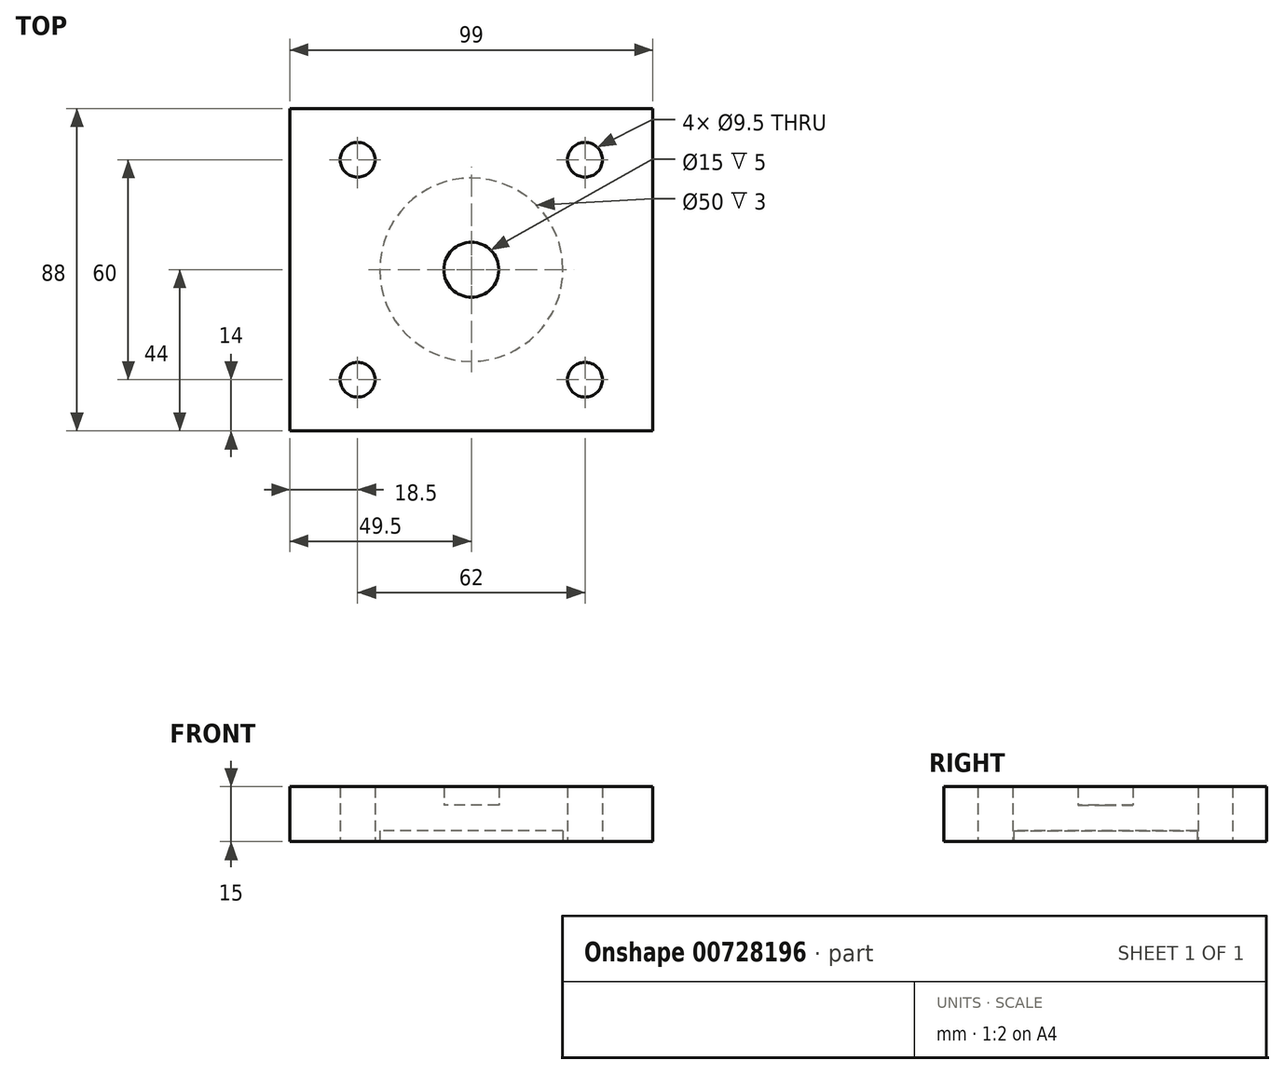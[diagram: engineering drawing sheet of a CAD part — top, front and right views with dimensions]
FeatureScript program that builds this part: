
annotation { "Feature Type Name" : "Feature", "Feature Type Description" : "" }
export const myFeature = defineFeature(function(context is Context, id is Id, definition is map)
    precondition{}
    {
        {
            var Q0;
            Q0=qCreatedBy(makeId("Top.planeOp"),FACE);
            var sketch = newSketch(context, id + "F0", { "sketchPlane" : qUnion([Q0])});
            skLineSegment(sketch, "E0.bottom", {"start": v(49.5, -44) * mm, "end": v(-49.5, -44) * mm});
            skLineSegment(sketch, "E0.top", {"start": v(49.5, 44) * mm, "end": v(-49.5, 44) * mm});
            skLineSegment(sketch, "E0.left", {"start": v(49.5, -44) * mm, "end": v(49.5, 44) * mm});
            skLineSegment(sketch, "E0.right", {"start": v(-49.5, -44) * mm, "end": v(-49.5, 44) * mm});
            skPoint(sketch, "E0.middle", {"position": v(0, 0) * mm});
            skCircle(sketch, "E1", {"center": v(-31, 30) * mm, "radius": 4.75 * mm});
            skCircle(sketch, "E2", {"center": v(31, 30) * mm, "radius": 4.75 * mm});
            skCircle(sketch, "E3.MirrorC", {"center": v(-31, -30) * mm, "radius": 4.75 * mm});
            skCircle(sketch, "E4.MirrorC", {"center": v(31, -30) * mm, "radius": 4.75 * mm});
            skCircle(sketch, "E5", {"center": v(0, 0) * mm, "radius": 7.5 * mm});
            skSolve(sketch);
        }
        {
            var Q0;
            Q0=makeQuery(id+"F0.imprint","IMPRINT",FACE,{"disambiguationData":[TD([[makeQuery(id+"F0.imprint","IMPRINT",EDGE,{"derivedFrom":sQuery(id+"F0.wireOp",EDGE,"E5")}),1.0]])]});
            extrude(context, id + "F1", {"entities" : qUnion([Q0]), "depth" : 10 * mm, "offsetDistance" : 25 * mm});
        }
        {
            var Q0;
            Q0=makeQuery(id+"F0.imprint","IMPRINT",FACE,{"disambiguationData":[TD([[makeQuery(id+"F0.imprint","IMPRINT",EDGE,{"derivedFrom":sQuery(id+"F0.wireOp",EDGE,"E0.bottom")}),-1.0]])]});
            extrude(context, id + "F2", {"entities" : qUnion([Q0]), "operationType" : NewBodyOperationType.ADD, "depth" : 15 * mm, "offsetDistance" : 25 * mm});
        }
        {
            var Q0;
            Q0=makeQuery(id+"F0.imprint","IMPRINT",FACE,{"disambiguationData":[TD([[makeQuery(id+"F0.imprint","IMPRINT",EDGE,{"derivedFrom":sQuery(id+"F0.wireOp",EDGE,"E0.bottom")}),-1.0]])]});
            var sketch = newSketch(context, id + "F3", { "sketchPlane" : qUnion([Q0])});
            skCircle(sketch, "E6", {"center": v(0, 0) * mm, "radius": 25 * mm});
            skSolve(sketch);
        }
        {
            var Q0;
            Q0=makeQuery(id+"F3.imprint","IMPRINT",FACE,{"disambiguationData":[TD([[makeQuery(id+"F3.imprint","IMPRINT",EDGE,{"derivedFrom":sQuery(id+"F3.wireOp",EDGE,"E6")}),1.0]])]});
            var Q1;
            Q1=makeQuery(id+"F0.imprint","IMPRINT",FACE,{"disambiguationData":[TD([[makeQuery(id+"F0.imprint","IMPRINT",EDGE,{"derivedFrom":sQuery(id+"F0.wireOp",EDGE,"E5")}),1.0]])]});
            extrude(context, id + "F4", {"entities" : qUnion([Q0, Q1]), "operationType" : NewBodyOperationType.REMOVE, "depth" : 3 * mm, "offsetDistance" : 25 * mm});
        }
    });
